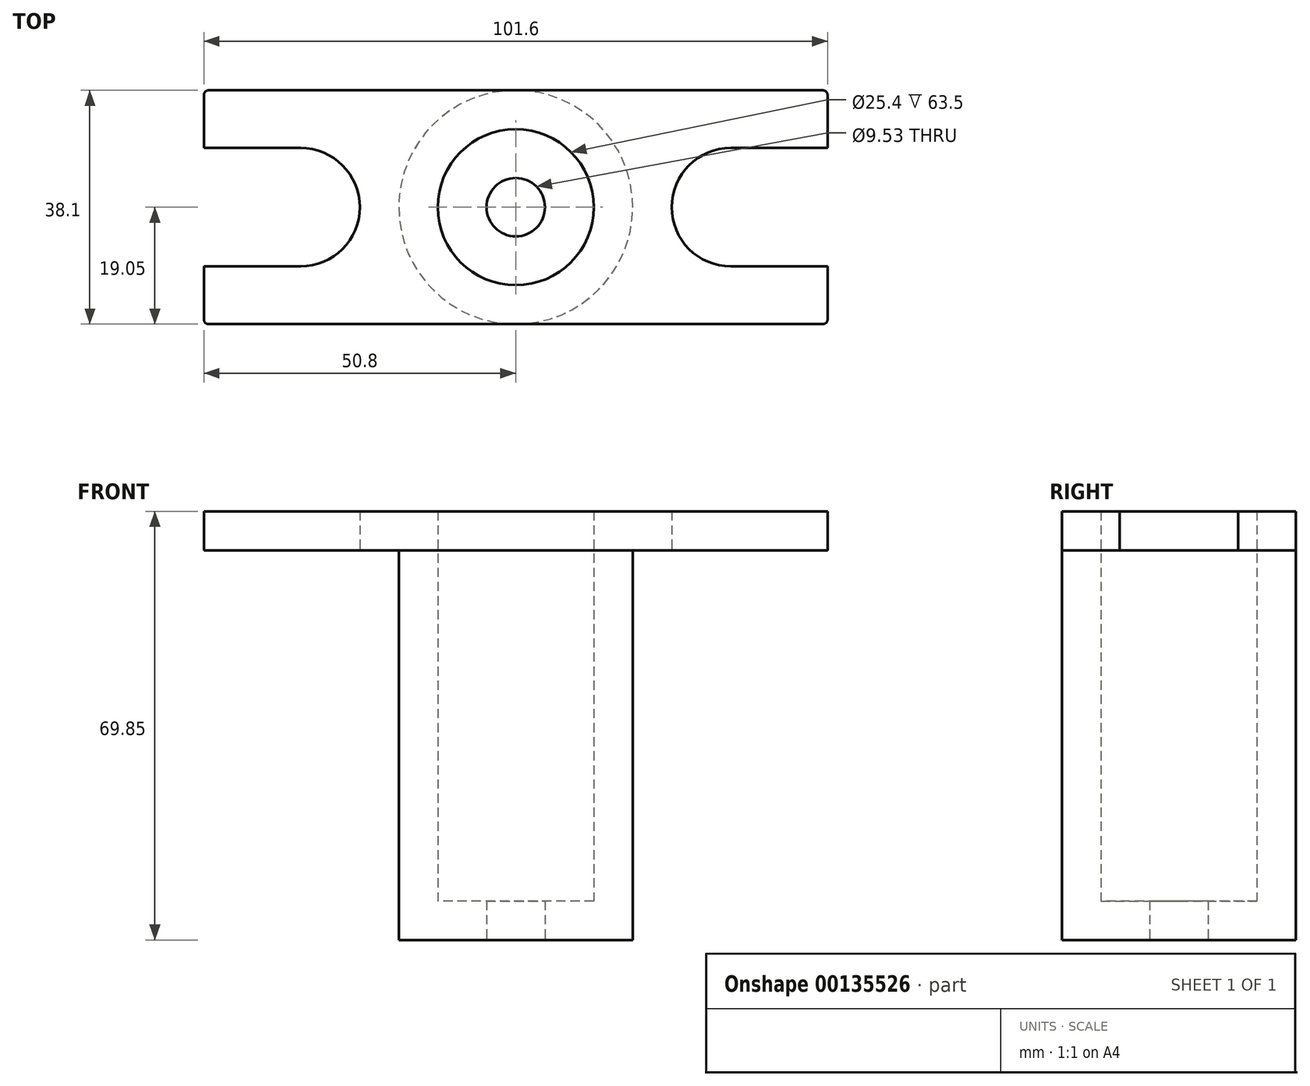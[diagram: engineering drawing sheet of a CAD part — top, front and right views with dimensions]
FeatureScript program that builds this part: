
annotation { "Feature Type Name" : "Feature", "Feature Type Description" : "" }
export const myFeature = defineFeature(function(context is Context, id is Id, definition is map)
    precondition{}
    {
        {
            var Q0;
            Q0=qCreatedBy(makeId("Top.planeOp"),FACE);
            var sketch = newSketch(context, id + "F0", { "sketchPlane" : qUnion([Q0])});
            skLineSegment(sketch, "E0.bottom", {"start": v(50.04, -19.05) * mm, "end": v(-50.04, -19.05) * mm});
            skLineSegment(sketch, "E0.top", {"start": v(50.04, 19.05) * mm, "end": v(-50.04, 19.05) * mm});
            skLineSegment(sketch, "E0.left", {"start": v(50.8, -18.29) * mm, "end": v(50.8, 18.29) * mm});
            skLineSegment(sketch, "E0.right", {"start": v(-50.8, -18.29) * mm, "end": v(-50.8, 18.29) * mm});
            skPoint(sketch, "E0.middle", {"position": v(0, 0) * mm});
            skCircle(sketch, "E1", {"center": v(0, 0) * mm, "radius": 12.7 * mm});
            skLineSegment(sketch, "E2", {"start": v(50.8, 9.65) * mm, "end": v(35.05, 9.65) * mm});
            skLineSegment(sketch, "E3", {"start": v(35.05, -9.65) * mm, "end": v(50.8, -9.65) * mm});
            skLineSegment(sketch, "E4", {"start": v(-50.8, 9.65) * mm, "end": v(-35.05, 9.65) * mm});
            skLineSegment(sketch, "E5", {"start": v(-35.05, -9.65) * mm, "end": v(-50.8, -9.65) * mm});
            skArc(sketch, "E6", {"start": v(-35.05, -9.65) * mm, "mid": v(-25.4, 0) * mm, "end": v(-35.05, 9.65) * mm});
            skArc(sketch, "E7", {"start": v(35.05, 9.65) * mm, "mid": v(25.4, 0) * mm, "end": v(35.05, -9.65) * mm});
            skCircle(sketch, "E8", {"center": v(0, 0) * mm, "radius": 19.05 * mm});
            skPoint(sketch, "E9.visualSharp", {"position": v(-50.8, 19.05) * mm});
            skArc(sketch, "E9.filletArc", {"start": v(-50.04, 19.05) * mm, "mid": v(-50.58, 18.83) * mm, "end": v(-50.8, 18.29) * mm});
            skPoint(sketch, "E10.visualSharp", {"position": v(-50.8, -19.05) * mm});
            skArc(sketch, "E10.filletArc", {"start": v(-50.8, -18.29) * mm, "mid": v(-50.58, -18.83) * mm, "end": v(-50.04, -19.05) * mm});
            skPoint(sketch, "E11.visualSharp", {"position": v(50.8, -19.05) * mm});
            skArc(sketch, "E11.filletArc", {"start": v(50.04, -19.05) * mm, "mid": v(50.58, -18.83) * mm, "end": v(50.8, -18.29) * mm});
            skPoint(sketch, "E12.visualSharp", {"position": v(50.8, 19.05) * mm});
            skArc(sketch, "E12.filletArc", {"start": v(50.8, 18.29) * mm, "mid": v(50.58, 18.83) * mm, "end": v(50.04, 19.05) * mm});
            skSolve(sketch);
        }
        {
            var Q0;
            Q0=makeQuery(id+"F0.imprint","IMPRINT",FACE,{"disambiguationData":[TD([[makeQuery(id+"F0.imprint","IMPRINT",EDGE,{"derivedFrom":sQuery(id+"F0.wireOp",EDGE,"E0.bottom")}),-1.0]])]});
            var Q1;
            Q1=makeQuery(id+"F0.imprint","IMPRINT",FACE,{"disambiguationData":[TD([[makeQuery(id+"F0.imprint","IMPRINT",EDGE,{"derivedFrom":sQuery(id+"F0.wireOp",EDGE,"E1")}),-1.0]])]});
            extrude(context, id + "F1", {"entities" : qUnion([Q0, Q1]), "depth" : 6.35 * mm});
        }
        {
            var Q0;
            Q0=makeQuery(id+"F0.imprint","IMPRINT",FACE,{"disambiguationData":[TD([[makeQuery(id+"F0.imprint","IMPRINT",EDGE,{"derivedFrom":sQuery(id+"F0.wireOp",EDGE,"E1")}),-1.0]])]});
            var Q1;
            Q1=makeQuery(id+"F0.imprint","IMPRINT",FACE,{"disambiguationData":[TD([[makeQuery(id+"F0.imprint","IMPRINT",EDGE,{"derivedFrom":sQuery(id+"F0.wireOp",EDGE,"E1")}),1.0]])]});
            extrude(context, id + "F2", {"entities" : qUnion([Q0, Q1]), "operationType" : NewBodyOperationType.ADD, "oppositeDirection" : true, "depth" : 63.5 * mm});
        }
        {
            var Q0;
            Q0=makeQuery(id+"F2.opExtrude","CAP_FACE",FACE,{"disambiguationData":[OSD([sQuery(id+"F0.wireOp",EDGE,"E8")])],"isStart":true});
            var Q1;
            Q1=sQuery(id+"F0.wireOp",EDGE,"E1");
            extrude(context, id + "F3", {"entities" : qUnion([Q0]), "operationType" : NewBodyOperationType.REMOVE, "surfaceEntities" : qUnion([Q1]), "oppositeDirection" : true, "depth" : 57.15 * mm});
        }
        {
            var Q0;
            Q0=makeQuery(id+"F2.opExtrude","CAP_FACE",FACE,{"disambiguationData":[OSD([sQuery(id+"F0.wireOp",EDGE,"E8")])],"isStart":false});
            var sketch = newSketch(context, id + "F4", { "sketchPlane" : qUnion([Q0])});
            skCircle(sketch, "E13", {"center": v(0, 0) * mm, "radius": 4.76 * mm});
            skSolve(sketch);
        }
        {
            var Q0;
            Q0=makeQuery(id+"F4.imprint","IMPRINT",FACE,{"disambiguationData":[TD([[makeQuery(id+"F4.imprint","IMPRINT",EDGE,{"derivedFrom":sQuery(id+"F4.wireOp",EDGE,"E13")}),1.0]])]});
            var Q1;
            Q1=sQuery(id+"F4.wireOp",EDGE,"E13");
            extrude(context, id + "F5", {"entities" : qUnion([Q0]), "operationType" : NewBodyOperationType.REMOVE, "surfaceEntities" : qUnion([Q1]), "oppositeDirection" : true, "depth" : 6.35 * mm});
        }
    });
